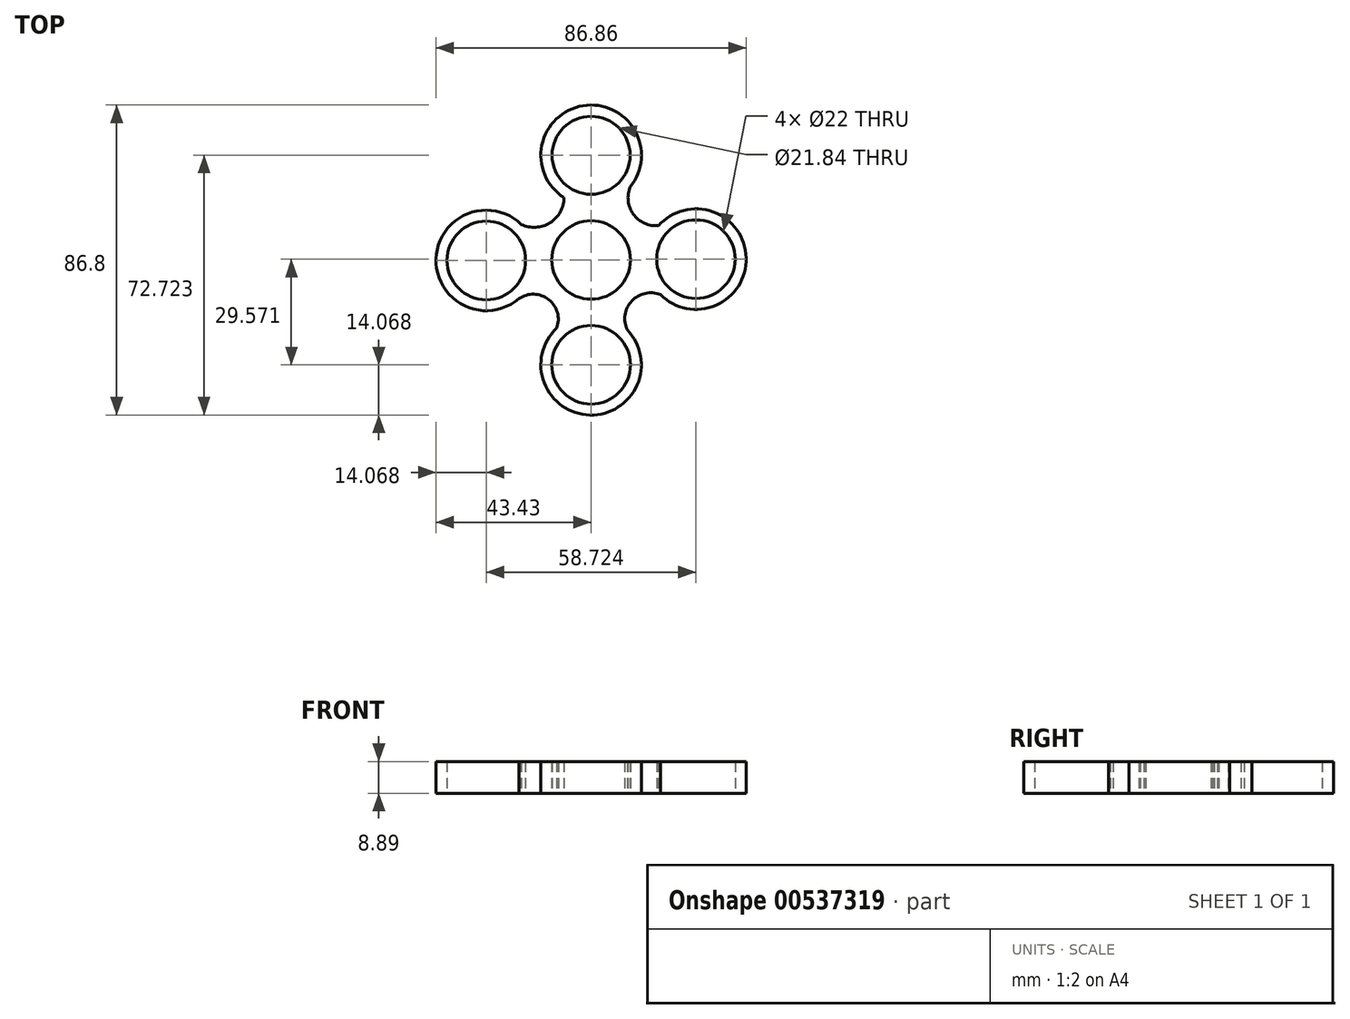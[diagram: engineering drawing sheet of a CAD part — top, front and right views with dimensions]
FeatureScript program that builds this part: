
annotation { "Feature Type Name" : "Feature", "Feature Type Description" : "" }
export const myFeature = defineFeature(function(context is Context, id is Id, definition is map)
    precondition{}
    {
        {
            var Q0;
            Q0=qCreatedBy(makeId("Top.planeOp"),FACE);
            var sketch = newSketch(context, id + "F0", { "sketchPlane" : qUnion([Q0])});
            skCircle(sketch, "E0", {"center": v(0, 0) * mm, "radius": 11 * mm});
            skCircle(sketch, "E1", {"center": v(0, 29.3) * mm, "radius": 10.92 * mm});
            skCircle(sketch, "E2", {"center": v(-29.36, -0.15) * mm, "radius": 11 * mm});
            skCircle(sketch, "E3", {"center": v(29.36, 0.2) * mm, "radius": 11 * mm});
            skCircle(sketch, "E4", {"center": v(0, -29.36) * mm, "radius": 11 * mm});
            skArc(sketch, "E5", {"start": v(10.96, 20.47) * mm, "mid": v(-2.26, 43.18) * mm, "end": v(-7.6, 17.44) * mm});
            skArc(sketch, "E6", {"start": v(19.4, -9.74) * mm, "mid": v(43.43, 0.6) * mm, "end": v(18.87, 9.59) * mm});
            skArc(sketch, "E7", {"start": v(-19.55, 9.94) * mm, "mid": v(-43.43, 0.3) * mm, "end": v(-20.2, -10.83) * mm});
            skArc(sketch, "E8", {"start": v(-9.66, -19.13) * mm, "mid": v(-0.33, -43.43) * mm, "end": v(10.14, -19.6) * mm});
            skArc(sketch, "E9", {"start": v(-9.66, -19.13) * mm, "mid": v(-11.88, -11.1) * mm, "end": v(-20.2, -10.83) * mm});
            skArc(sketch, "E10", {"start": v(-19.55, 9.94) * mm, "mid": v(-11.5, 10.4) * mm, "end": v(-7.6, 17.44) * mm});
            skArc(sketch, "E11", {"start": v(10.96, 20.47) * mm, "mid": v(11.84, 12.8) * mm, "end": v(18.87, 9.59) * mm});
            skArc(sketch, "E12", {"start": v(19.4, -9.74) * mm, "mid": v(11.39, -11.49) * mm, "end": v(10.14, -19.6) * mm});
            skSolve(sketch);
        }
        {
            var Q0;
            Q0 = qSketchRegion(id + "F0", true);
            extrude(context, id + "F1", {"entities" : qUnion([Q0]), "depth" : 8.9 * mm, "offsetDistance" : 25.4 * mm});
        }
    });
